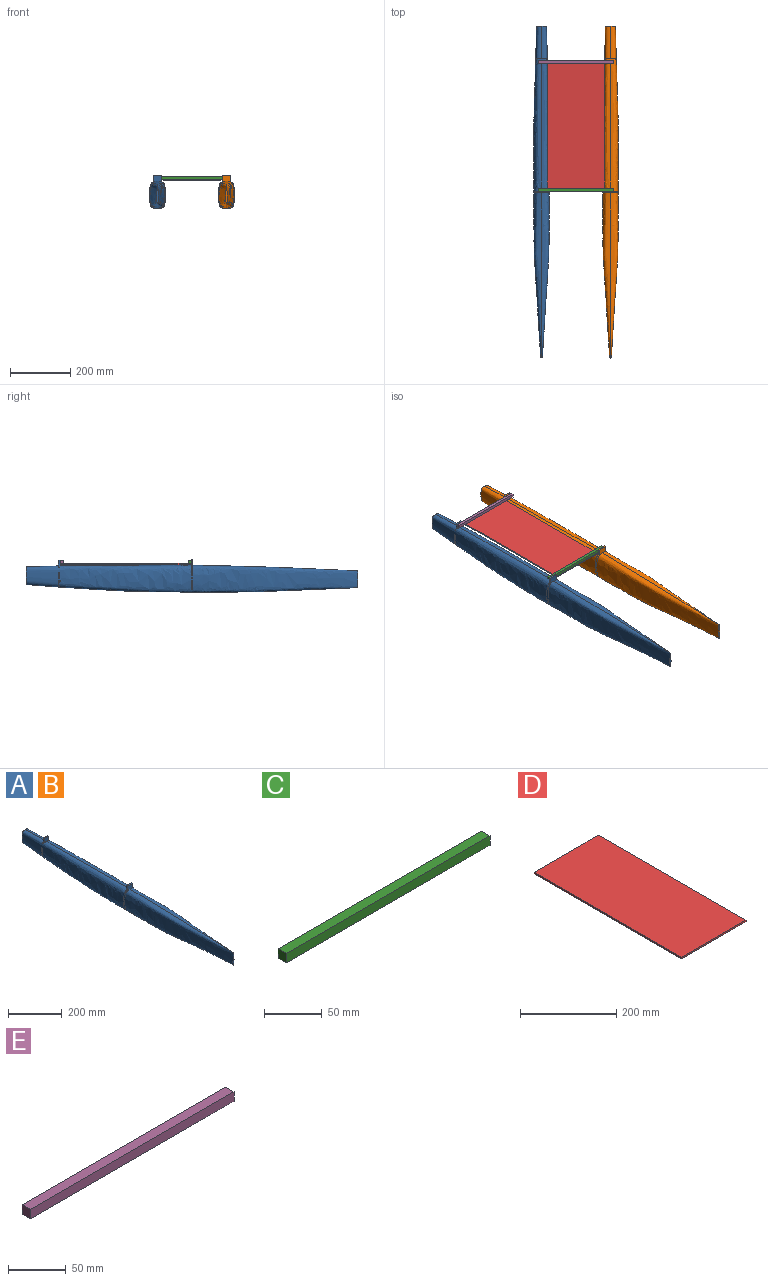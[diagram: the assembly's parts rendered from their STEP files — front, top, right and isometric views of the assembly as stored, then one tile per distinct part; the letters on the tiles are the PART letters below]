
ASSEMBLY  parts=5 mates=5
PART A: 57 faces, bbox 55.6x1101.7x110.5 mm
  f0: plane 55.77x5.57mm, normal (0,-1,0), area 239.3mm2, adj f2,f3
  f1: plane 58.79x33.15mm, normal (0,1,0), area 1714.8mm2, adj f2,f3
  f2: bspline ~1100x91.13mm, area 114735mm2, adj f0,f1,f3,f4,f5,f8,f19,f20
  f3: bspline ~1100x90.17mm, area 114744.1mm2, adj f0,f1,f2,f4,f5,f6,f9,f10
  f4: plane 21.83x19.89mm, normal (0,1,0), area 405.5mm2, adj f2,f3,f6,f7,f8
  f5: plane 21.82x19.69mm, normal (0,-1,0), area 401.9mm2, adj f2,f3,f6,f7,f8
  f6: plane 19.68x6mm, normal (-1,0,0), area 117.5mm2, adj f3,f4,f5,f7
  f7: plane 21.62x6mm, normal (0,0,1), area 129.7mm2, adj f4,f5,f6,f8
  f8: plane 19.68x6mm, normal (1,0,0), area 117.5mm2, adj f2,f4,f5,f7
  f9: plane 2.38x2.3mm, normal (0,1,0), area 0.2mm2, adj f3,f10,f11
  f10: plane 2.84x0.08mm, normal (-0.32,0,-0.95), area 0.1mm2, adj f3,f9,f11
  f11: extruded ~3.55x2.3mm, area 8.3mm2, adj f3,f9,f10
  f12: plane 20.63x0.35mm, normal (0,1,0), area 2.7mm2, adj f3,f13,f14
  f13: plane 5.4x0.17mm, normal (0,0,-1), area 0.4mm2, adj f3,f12,f14
  f14: extruded ~20.51x5.47mm, area 92.8mm2, adj f3,f12,f13
  f15: plane 22.54x16.13mm, normal (0,1,0), area 6.8mm2, adj f3,f16,f17,f18
  f16: plane 3.53x0.26mm, normal (1,0,0), area 0.5mm2, adj f3,f15,f17
  f17: extruded ~22.53x16.13mm, area 122.4mm2, adj f3,f15,f16,f18
  f18: plane 5.59x0.19mm, normal (0,0,1), area 0.5mm2, adj f3,f15,f17
  f19: plane 4.31x0.53mm, normal (0,-1,0), area 0mm2, adj f2,f21,f22
  f20: plane 22.55x16.41mm, normal (0,1,0), area 7.3mm2, adj f2,f21,f22,f23
  f21: plane 6x0.21mm, normal (0,0,1), area 0.6mm2, adj f2,f19,f20,f22
  f22: extruded ~22.54x16.41mm, area 132.6mm2, adj f2,f19,f20,f21,f23
  f23: plane 3.43x0.25mm, normal (-1,0,0), area 0.4mm2, adj f2,f20,f22
  f24: plane 20.53x0.36mm, normal (0,1,0), area 2.8mm2, adj f2,f25,f26
  f25: extruded ~20.42x5.79mm, area 95.2mm2, adj f2,f24,f26
  f26: plane 5.79x0.18mm, normal (0,0,-1), area 0.5mm2, adj f2,f24,f25
  f27: plane 2.38x2.28mm, normal (0,1,0), area 0.2mm2, adj f2,f28,f29
  f28: plane 2.58x0.07mm, normal (0.32,0,-0.95), area 0.1mm2, adj f2,f27,f29
  f29: extruded ~3.32x2.27mm, area 7.6mm2, adj f2,f27,f28
  f30: extruded ~8.08x7.73mm, area 67.9mm2, adj f31,f35,f36,f38
  f31: plane 20.48x6mm, normal (1,0,0), area 122.9mm2, adj f30,f32,f35,f36
  f32: plane 28.23x6mm, normal (0,0,1), area 169.4mm2, adj f31,f33,f35,f36
  f33: plane 20.48x6mm, normal (-1,0,0), area 122.9mm2, adj f32,f34,f35,f36
  f34: extruded ~8.05x7.72mm, area 67.7mm2, adj f33,f35,f36,f37
  f35: plane 44.69x29.71mm, normal (0,-1,0), area 552.5mm2, adj f2,f3,f30,f31,f32,f33,f34,f37
  f36: plane 44.9x29.92mm, normal (0,1,0), area 550.6mm2, adj f2,f3,f30,f31,f32,f33,f34,f37
  f37: plane 6x0.4mm, normal (-0.32,0,-0.95), area 2.5mm2, adj f3,f34,f35,f36
  f38: plane 6x0.36mm, normal (0.32,0,-0.95), area 2.2mm2, adj f2,f30,f35,f36
  f39: extruded ~28.04x6mm, area 169.4mm2, adj f40,f41,f42,f43
  f40: plane 29.68x4.85mm, normal (0,-1,0), area 9mm2, adj f3,f39,f42,f43
  f41: plane 29.59x4.76mm, normal (0,1,0), area 8.5mm2, adj f3,f39,f42,f43
  f42: plane 6x0.44mm, normal (0,0,-1), area 2.5mm2, adj f3,f39,f40,f41
  f43: plane 6x0.48mm, normal (0.32,0,0.95), area 3mm2, adj f3,f39,f40,f41
  f44: plane 33.66x6.21mm, normal (0,-1,0), area 18.6mm2, adj f3,f46,f47
  f45: plane 33.6x6.31mm, normal (0,1,0), area 16.7mm2, adj f3,f46,f47
  f46: extruded ~32.07x6mm, area 194.7mm2, adj f3,f44,f45,f47
  f47: plane 6x0.5mm, normal (0,0,1), area 2.8mm2, adj f3,f44,f45,f46
  f48: plane 33.21x5.99mm, normal (0,-1,0), area 17mm2, adj f2,f50,f51
  f49: plane 33.15x6.08mm, normal (0,1,0), area 15.4mm2, adj f2,f50,f51
  f50: plane 6x0.45mm, normal (0,0,1), area 2.6mm2, adj f2,f48,f49,f51
  f51: extruded ~31.66x6mm, area 192.1mm2, adj f2,f48,f49,f50
  f52: plane 29.63x4.78mm, normal (0,-1,0), area 7.6mm2, adj f2,f54,f55,f56
  f53: plane 29.55x4.69mm, normal (0,1,0), area 7.2mm2, adj f2,f54,f55,f56
  f54: plane 6x0.39mm, normal (0,0,-1), area 2.2mm2, adj f2,f52,f53,f55
  f55: extruded ~28.01x6mm, area 169.2mm2, adj f52,f53,f54,f56
  f56: plane 6x0.44mm, normal (-0.32,0,0.95), area 2.7mm2, adj f2,f52,f53,f55
PART B: same geometry as A
PART C: 6 faces, bbox 250x10x10 mm
  f0: plane 10x10mm, normal (1,0,0), area 100mm2, adj f1,f3,f4,f5
  f1: plane 250x10mm, normal (0,1,0), area 2500mm2, adj f0,f2,f4,f5
  f2: plane 10x10mm, normal (-1,0,0), area 100mm2, adj f1,f3,f4,f5
  f3: plane 250x10mm, normal (0,-1,0), area 2500mm2, adj f0,f2,f4,f5
  f4: plane 250x10mm, normal (0,0,1), area 2500mm2, adj f0,f1,f2,f3
  f5: plane 250x10mm, normal (0,0,-1), area 2500mm2, adj f0,f1,f2,f3
PART D: 6 faces, bbox 190x434x4 mm
  f0: plane 434x4mm, normal (-1,0,0), area 1736mm2, adj f1,f3,f4,f5
  f1: plane 190x4mm, normal (0,-1,0), area 760mm2, adj f0,f2,f4,f5
  f2: plane 434x4mm, normal (1,0,0), area 1736mm2, adj f1,f3,f4,f5
  f3: plane 190x4mm, normal (0,1,0), area 760mm2, adj f0,f2,f4,f5
  f4: plane 434x190mm, normal (0,0,-1), area 82460mm2, adj f0,f1,f2,f3
  f5: plane 434x190mm, normal (0,0,1), area 82460mm2, adj f0,f1,f2,f3
PART E: 6 faces, bbox 250x10x10 mm
  f0: plane 10x10mm, normal (-1,0,0), area 100mm2, adj f1,f3,f4,f5
  f1: plane 250x10mm, normal (0,-1,0), area 2500mm2, adj f0,f2,f4,f5
  f2: plane 10x10mm, normal (1,0,0), area 100mm2, adj f1,f3,f4,f5
  f3: plane 250x10mm, normal (0,1,0), area 2500mm2, adj f0,f2,f4,f5
  f4: plane 250x10mm, normal (0,0,1), area 2500mm2, adj f0,f1,f2,f3
  f5: plane 250x10mm, normal (0,0,-1), area 2500mm2, adj f0,f1,f2,f3
PLACE A t=(-254.87,-555.03,-56.02)mm
PLACE B t=(-26.49,-555.03,-56.02)mm
PLACE C t=(-237.54,-2.03,44.84)mm
PLACE D t=(-237.54,-2.03,44.84)mm
PLACE E t=(-237.54,-2.03,44.84)mm
MATE fastened D.f5 <-> C.f5  axis (0,0,1) through (-17.54,-2.03,44.84)mm
MATE fastened E.f3 <-> E.f3  axis (0,1,0) through (12.46,431.97,54.84)mm
MATE fastened E.f3 <-> A.f5  axis (0,1,0) through (-237.54,431.97,54.84)mm
MATE fastened D.f5 <-> E.f5  axis (0,0,1) through (-17.54,431.97,44.84)mm
MATE fastened E.f3 <-> B.f5  axis (0,1,0) through (12.46,431.97,54.84)mm
